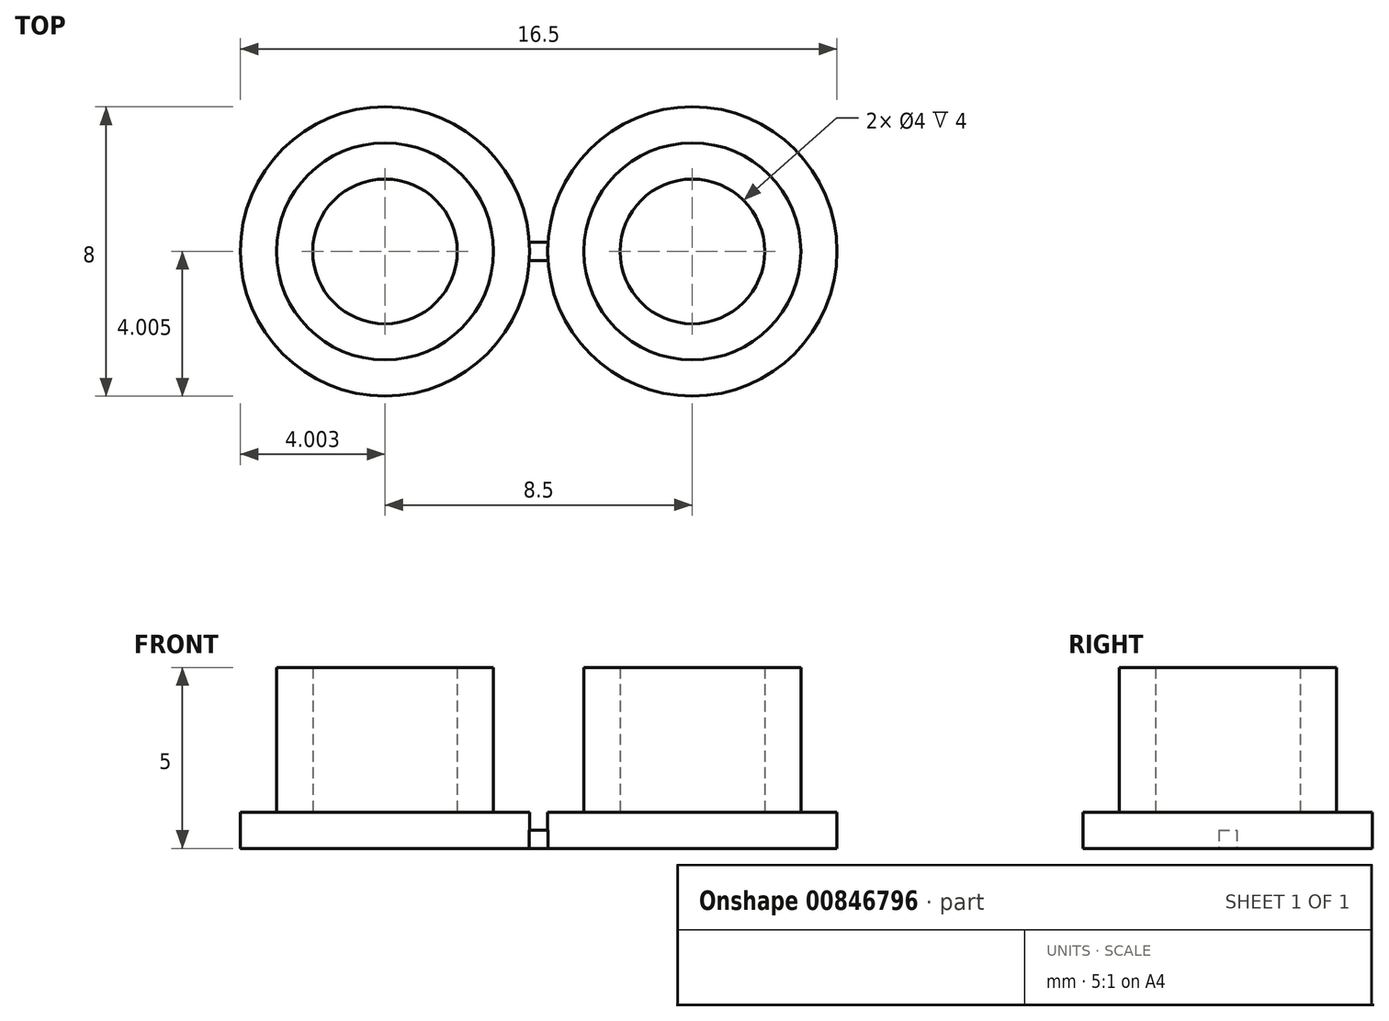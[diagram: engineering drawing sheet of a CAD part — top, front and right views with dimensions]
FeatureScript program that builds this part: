
annotation { "Feature Type Name" : "Feature", "Feature Type Description" : "" }
export const myFeature = defineFeature(function(context is Context, id is Id, definition is map)
    precondition{}
    {
        {
            var Q0;
            Q0=qCreatedBy(makeId("Top.planeOp"),FACE);
            var sketch = newSketch(context, id + "F0", { "sketchPlane" : qUnion([Q0])});
            skCircle(sketch, "E0", {"center": v(-46.83, 34.3) * mm, "radius": 2 * mm});
            skCircle(sketch, "E1", {"center": v(-46.83, 34.3) * mm, "radius": 3 * mm});
            skCircle(sketch, "E2", {"center": v(-46.83, 34.3) * mm, "radius": 4 * mm});
            skCircle(sketch, "E3.1.0.0", {"center": v(-38.33, 34.3) * mm, "radius": 4 * mm});
            skCircle(sketch, "E3.1.0.1", {"center": v(-38.33, 34.3) * mm, "radius": 3 * mm});
            skCircle(sketch, "E3.1.0.2", {"center": v(-38.33, 34.3) * mm, "radius": 2 * mm});
            skLineSegment(sketch, "E3.direction1", {"start": v(-46.83, 34.3) * mm, "end": v(-38.33, 34.3) * mm, "construction": true});
            skLineSegment(sketch, "E3.direction2", {"start": v(-46.83, 34.3) * mm, "end": v(-46.83, 42.8) * mm, "construction": true});
            skPoint(sketch, "E4", {"position": v(-42.58, 34.3) * mm});
            skLineSegment(sketch, "E5.bottom", {"start": v(-42.83, 34.54) * mm, "end": v(-42.32, 34.54) * mm});
            skLineSegment(sketch, "E5.top", {"start": v(-42.83, 34.05) * mm, "end": v(-42.32, 34.05) * mm});
            skSolve(sketch);
        }
        {
            var Q0;
            Q0=makeQuery(id+"F0.imprint","IMPRINT",FACE,{"disambiguationData":[TD([[makeQuery(id+"F0.imprint","IMPRINT",EDGE,{"derivedFrom":sQuery(id+"F0.wireOp",EDGE,"E0")}),-1.0]])]});
            var Q1;
            Q1=makeQuery(id+"F0.imprint","IMPRINT",FACE,{"disambiguationData":[TD([[makeQuery(id+"F0.imprint","IMPRINT",EDGE,{"derivedFrom":sQuery(id+"F0.wireOp",EDGE,"E3.0.1.1")}),1.0]])]});
            var Q2;
            Q2=makeQuery(id+"F0.imprint","IMPRINT",FACE,{"disambiguationData":[TD([[makeQuery(id+"F0.imprint","IMPRINT",EDGE,{"derivedFrom":sQuery(id+"F0.wireOp",EDGE,"E3.0.2.1")}),1.0]])]});
            var Q3;
            Q3=makeQuery(id+"F0.imprint","IMPRINT",FACE,{"disambiguationData":[TD([[makeQuery(id+"F0.imprint","IMPRINT",EDGE,{"derivedFrom":sQuery(id+"F0.wireOp",EDGE,"E3.1.2.1")}),1.0]])]});
            var Q4;
            Q4=makeQuery(id+"F0.imprint","IMPRINT",FACE,{"disambiguationData":[TD([[makeQuery(id+"F0.imprint","IMPRINT",EDGE,{"derivedFrom":sQuery(id+"F0.wireOp",EDGE,"E3.2.2.1")}),1.0]])]});
            var Q5;
            Q5=makeQuery(id+"F0.imprint","IMPRINT",FACE,{"disambiguationData":[TD([[makeQuery(id+"F0.imprint","IMPRINT",EDGE,{"derivedFrom":sQuery(id+"F0.wireOp",EDGE,"E3.3.2.1")}),1.0]])]});
            var Q6;
            Q6=makeQuery(id+"F0.imprint","IMPRINT",FACE,{"disambiguationData":[TD([[makeQuery(id+"F0.imprint","IMPRINT",EDGE,{"derivedFrom":sQuery(id+"F0.wireOp",EDGE,"E3.3.1.1")}),1.0]])]});
            var Q7;
            Q7=makeQuery(id+"F0.imprint","IMPRINT",FACE,{"disambiguationData":[TD([[makeQuery(id+"F0.imprint","IMPRINT",EDGE,{"derivedFrom":sQuery(id+"F0.wireOp",EDGE,"E3.2.1.1")}),1.0]])]});
            var Q8;
            Q8=makeQuery(id+"F0.imprint","IMPRINT",FACE,{"disambiguationData":[TD([[makeQuery(id+"F0.imprint","IMPRINT",EDGE,{"derivedFrom":sQuery(id+"F0.wireOp",EDGE,"E3.1.1.1")}),1.0]])]});
            var Q9;
            Q9=makeQuery(id+"F0.imprint","IMPRINT",FACE,{"disambiguationData":[TD([[makeQuery(id+"F0.imprint","IMPRINT",EDGE,{"derivedFrom":sQuery(id+"F0.wireOp",EDGE,"E3.1.0.1")}),1.0]])]});
            var Q10;
            Q10=makeQuery(id+"F0.imprint","IMPRINT",FACE,{"disambiguationData":[TD([[makeQuery(id+"F0.imprint","IMPRINT",EDGE,{"derivedFrom":sQuery(id+"F0.wireOp",EDGE,"E3.2.0.1")}),1.0]])]});
            var Q11;
            Q11=makeQuery(id+"F0.imprint","IMPRINT",FACE,{"disambiguationData":[TD([[makeQuery(id+"F0.imprint","IMPRINT",EDGE,{"derivedFrom":sQuery(id+"F0.wireOp",EDGE,"E3.3.0.1")}),1.0]])]});
            extrude(context, id + "F1", {"entities" : qUnion([Q0, Q1, Q2, Q3, Q4, Q5, Q6, Q7, Q8, Q9, Q10, Q11]), "depth" : 5 * mm, "offsetDistance" : 25 * mm});
        }
        {
            var Q0;
            Q0=makeQuery(id+"F0.imprint","IMPRINT",FACE,{"disambiguationData":[TD([[makeQuery(id+"F0.imprint","IMPRINT",EDGE,{"derivedFrom":sQuery(id+"F0.wireOp",EDGE,"E1")}),-1.0]])]});
            var Q1;
            Q1=makeQuery(id+"F0.imprint","IMPRINT",FACE,{"disambiguationData":[TD([[makeQuery(id+"F0.imprint","IMPRINT",EDGE,{"derivedFrom":sQuery(id+"F0.wireOp",EDGE,"E0")}),1.0]])]});
            var Q2;
            Q2=makeQuery(id+"F0.imprint","IMPRINT",FACE,{"disambiguationData":[TD([[makeQuery(id+"F0.imprint","IMPRINT",EDGE,{"derivedFrom":sQuery(id+"F0.wireOp",EDGE,"E3.0.1.0")}),1.0]])]});
            var Q3;
            Q3=makeQuery(id+"F0.imprint","IMPRINT",FACE,{"disambiguationData":[TD([[makeQuery(id+"F0.imprint","IMPRINT",EDGE,{"derivedFrom":sQuery(id+"F0.wireOp",EDGE,"E3.0.1.2")}),1.0]])]});
            var Q4;
            Q4=makeQuery(id+"F0.imprint","IMPRINT",FACE,{"disambiguationData":[TD([[makeQuery(id+"F0.imprint","IMPRINT",EDGE,{"derivedFrom":sQuery(id+"F0.wireOp",EDGE,"E3.0.2.0")}),1.0]])]});
            var Q5;
            Q5=makeQuery(id+"F0.imprint","IMPRINT",FACE,{"disambiguationData":[TD([[makeQuery(id+"F0.imprint","IMPRINT",EDGE,{"derivedFrom":sQuery(id+"F0.wireOp",EDGE,"E3.0.2.2")}),1.0]])]});
            var Q6;
            Q6=makeQuery(id+"F0.imprint","IMPRINT",FACE,{"disambiguationData":[TD([[makeQuery(id+"F0.imprint","IMPRINT",EDGE,{"derivedFrom":sQuery(id+"F0.wireOp",EDGE,"E3.1.2.2")}),1.0]])]});
            var Q7;
            Q7=makeQuery(id+"F0.imprint","IMPRINT",FACE,{"disambiguationData":[TD([[makeQuery(id+"F0.imprint","IMPRINT",EDGE,{"derivedFrom":sQuery(id+"F0.wireOp",EDGE,"E3.1.2.0")}),1.0]])]});
            var Q8;
            Q8=makeQuery(id+"F0.imprint","IMPRINT",FACE,{"disambiguationData":[TD([[makeQuery(id+"F0.imprint","IMPRINT",EDGE,{"derivedFrom":sQuery(id+"F0.wireOp",EDGE,"E3.1.1.2")}),1.0]])]});
            var Q9;
            Q9=makeQuery(id+"F0.imprint","IMPRINT",FACE,{"disambiguationData":[TD([[makeQuery(id+"F0.imprint","IMPRINT",EDGE,{"derivedFrom":sQuery(id+"F0.wireOp",EDGE,"E3.1.0.0")}),1.0]])]});
            var Q10;
            Q10=makeQuery(id+"F0.imprint","IMPRINT",FACE,{"disambiguationData":[TD([[makeQuery(id+"F0.imprint","IMPRINT",EDGE,{"derivedFrom":sQuery(id+"F0.wireOp",EDGE,"E3.2.0.0")}),1.0]])]});
            var Q11;
            Q11=makeQuery(id+"F0.imprint","IMPRINT",FACE,{"disambiguationData":[TD([[makeQuery(id+"F0.imprint","IMPRINT",EDGE,{"derivedFrom":sQuery(id+"F0.wireOp",EDGE,"E3.2.0.2")}),1.0]])]});
            var Q12;
            Q12=makeQuery(id+"F0.imprint","IMPRINT",FACE,{"disambiguationData":[TD([[makeQuery(id+"F0.imprint","IMPRINT",EDGE,{"derivedFrom":sQuery(id+"F0.wireOp",EDGE,"E3.1.1.0")}),1.0]])]});
            var Q13;
            Q13=makeQuery(id+"F0.imprint","IMPRINT",FACE,{"disambiguationData":[TD([[makeQuery(id+"F0.imprint","IMPRINT",EDGE,{"derivedFrom":sQuery(id+"F0.wireOp",EDGE,"E3.2.1.0")}),1.0]])]});
            var Q14;
            Q14=makeQuery(id+"F0.imprint","IMPRINT",FACE,{"disambiguationData":[TD([[makeQuery(id+"F0.imprint","IMPRINT",EDGE,{"derivedFrom":sQuery(id+"F0.wireOp",EDGE,"E3.2.1.2")}),1.0]])]});
            var Q15;
            Q15=makeQuery(id+"F0.imprint","IMPRINT",FACE,{"disambiguationData":[TD([[makeQuery(id+"F0.imprint","IMPRINT",EDGE,{"derivedFrom":sQuery(id+"F0.wireOp",EDGE,"E3.3.0.0")}),1.0]])]});
            var Q16;
            Q16=makeQuery(id+"F0.imprint","IMPRINT",FACE,{"disambiguationData":[TD([[makeQuery(id+"F0.imprint","IMPRINT",EDGE,{"derivedFrom":sQuery(id+"F0.wireOp",EDGE,"E3.3.0.2")}),1.0]])]});
            var Q17;
            Q17=makeQuery(id+"F0.imprint","IMPRINT",FACE,{"disambiguationData":[TD([[makeQuery(id+"F0.imprint","IMPRINT",EDGE,{"derivedFrom":sQuery(id+"F0.wireOp",EDGE,"E3.3.1.2")}),1.0]])]});
            var Q18;
            Q18=makeQuery(id+"F0.imprint","IMPRINT",FACE,{"disambiguationData":[TD([[makeQuery(id+"F0.imprint","IMPRINT",EDGE,{"derivedFrom":sQuery(id+"F0.wireOp",EDGE,"E3.3.1.0")}),1.0]])]});
            var Q19;
            Q19=makeQuery(id+"F0.imprint","IMPRINT",FACE,{"disambiguationData":[TD([[makeQuery(id+"F0.imprint","IMPRINT",EDGE,{"derivedFrom":sQuery(id+"F0.wireOp",EDGE,"E3.3.2.0")}),1.0]])]});
            var Q20;
            Q20=makeQuery(id+"F0.imprint","IMPRINT",FACE,{"disambiguationData":[TD([[makeQuery(id+"F0.imprint","IMPRINT",EDGE,{"derivedFrom":sQuery(id+"F0.wireOp",EDGE,"E3.3.2.2")}),1.0]])]});
            var Q21;
            Q21=makeQuery(id+"F0.imprint","IMPRINT",FACE,{"disambiguationData":[TD([[makeQuery(id+"F0.imprint","IMPRINT",EDGE,{"derivedFrom":sQuery(id+"F0.wireOp",EDGE,"E3.2.2.0")}),1.0]])]});
            var Q22;
            Q22=makeQuery(id+"F0.imprint","IMPRINT",FACE,{"disambiguationData":[TD([[makeQuery(id+"F0.imprint","IMPRINT",EDGE,{"derivedFrom":sQuery(id+"F0.wireOp",EDGE,"E3.2.2.2")}),1.0]])]});
            var Q23;
            Q23=makeQuery(id+"F0.imprint","IMPRINT",FACE,{"disambiguationData":[TD([[makeQuery(id+"F0.imprint","IMPRINT",EDGE,{"derivedFrom":sQuery(id+"F0.wireOp",EDGE,"E3.1.0.2")}),1.0]])]});
            extrude(context, id + "F2", {"entities" : qUnion([Q0, Q1, Q2, Q3, Q4, Q5, Q6, Q7, Q8, Q9, Q10, Q11, Q12, Q13, Q14, Q15, Q16, Q17, Q18, Q19, Q20, Q21, Q22, Q23]), "operationType" : NewBodyOperationType.ADD, "depth" : 1 * mm, "offsetDistance" : 25 * mm});
        }
        {
            var Q0;
            {var subQ0=sQuery(id+"F0.wireOp",EDGE,"E5.bottom");Q0=makeQuery(id+"F0.imprint","IMPRINT",FACE,{"disambiguationData":[TD([[makeQuery(id+"F0.imprint","IMPRINT",EDGE,{"derivedFrom":subQ0}),-1.0]])]});}
            extrude(context, id + "F3", {"entities" : qUnion([Q0]), "depth" : 0.5 * mm, "offsetDistance" : 25 * mm});
        }
    });
